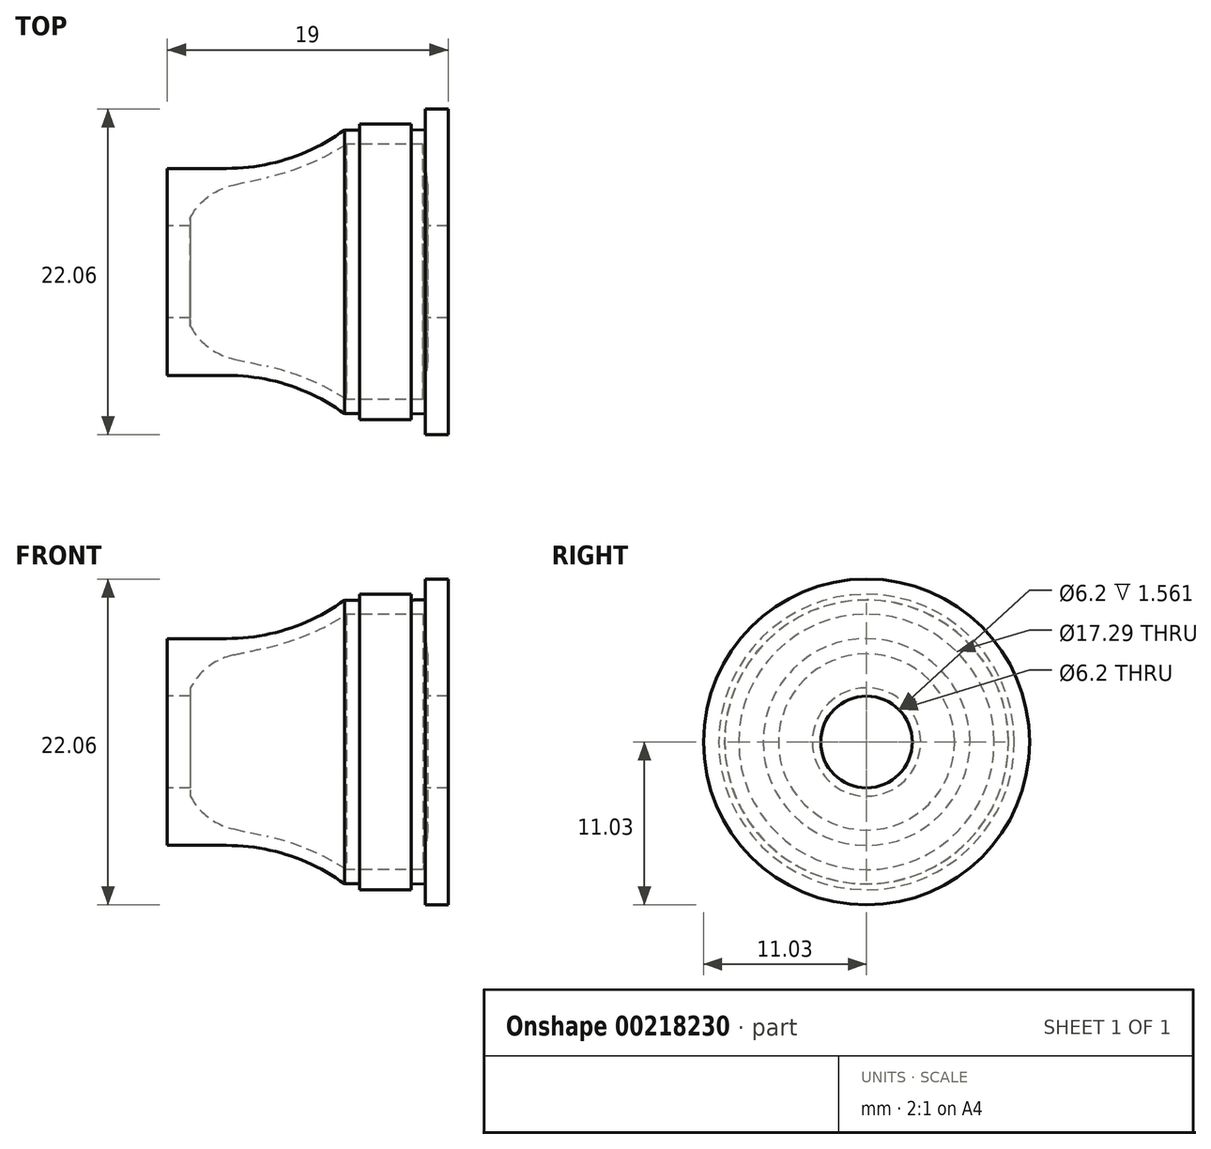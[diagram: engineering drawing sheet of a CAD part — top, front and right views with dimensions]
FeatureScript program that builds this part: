
annotation { "Feature Type Name" : "Feature", "Feature Type Description" : "" }
export const myFeature = defineFeature(function(context is Context, id is Id, definition is map)
    precondition{}
    {
        {
            var Q0;
            Q0=qCreatedBy(makeId("Top.planeOp"),FACE);
            var sketch = newSketch(context, id + "F0", { "sketchPlane" : qUnion([Q0])});
            skLineSegment(sketch, "E0", {"start": v(0, 7) * mm, "end": v(4.01, 7) * mm});
            skLineSegment(sketch, "E1", {"start": v(12, 9.6) * mm, "end": v(13, 9.6) * mm});
            skLineSegment(sketch, "E2", {"start": v(19, 11.03) * mm, "end": v(19, 3.1) * mm});
            skLineSegment(sketch, "E3", {"start": v(19, 3.1) * mm, "end": v(17.44, 3.1) * mm});
            skLineSegment(sketch, "E4", {"start": v(0, 3.1) * mm, "end": v(0, 7) * mm});
            skLineSegment(sketch, "E5", {"start": v(-2.93, 0) * mm, "end": v(20.9, 0) * mm, "construction": true});
            skLineSegment(sketch, "E6", {"start": v(0, 3.1) * mm, "end": v(1.56, 3.1) * mm});
            skLineSegment(sketch, "E7", {"start": v(1.56, 3.1) * mm, "end": v(1.56, 3.67) * mm});
            skLineSegment(sketch, "E8", {"start": v(12.14, 8.64) * mm, "end": v(17.3, 8.64) * mm});
            skLineSegment(sketch, "E9", {"start": v(1.56, 3.1) * mm, "end": v(0, 3.1) * mm});
            skLineSegment(sketch, "E10", {"start": v(16.5, 9.6) * mm, "end": v(16.5, 10) * mm});
            skLineSegment(sketch, "E11", {"start": v(16.5, 10) * mm, "end": v(13, 10) * mm});
            skLineSegment(sketch, "E12", {"start": v(13, 10) * mm, "end": v(13, 9.6) * mm});
            skLineSegment(sketch, "E13", {"start": v(16.5, 9.6) * mm, "end": v(17.5, 9.62) * mm});
            skLineSegment(sketch, "E14", {"start": v(4.5, 5.89) * mm, "end": v(6.76, 6.4) * mm});
            skArc(sketch, "E15", {"start": v(4.5, 5.89) * mm, "mid": v(2.78, 5.1) * mm, "end": v(1.56, 3.67) * mm});
            skLineSegment(sketch, "E16", {"start": v(17.63, 5.96) * mm, "end": v(17.44, 3.1) * mm});
            skArc(sketch, "E17", {"start": v(4.01, 7) * mm, "mid": v(8.21, 7.67) * mm, "end": v(12, 9.6) * mm});
            skArc(sketch, "E18", {"start": v(6.76, 6.4) * mm, "mid": v(9.55, 7.28) * mm, "end": v(12.14, 8.64) * mm});
            skLineSegment(sketch, "E19", {"start": v(17.3, 8.64) * mm, "end": v(17.63, 5.96) * mm});
            skLineSegment(sketch, "E20", {"start": v(17.5, 9.62) * mm, "end": v(17.47, 11.03) * mm});
            skLineSegment(sketch, "E21", {"start": v(17.47, 11.03) * mm, "end": v(19, 11.03) * mm});
            skSolve(sketch);
        }
        {
            var Q0;
            Q0=makeQuery(id+"F0.imprint","IMPRINT",FACE,{"disambiguationData":[TD([[makeQuery(id+"F0.imprint","IMPRINT",EDGE,{"derivedFrom":sQuery(id+"F0.wireOp",EDGE,"E0")}),-1.0]])]});
            var Q1;
            Q1=sQuery(id+"F0.wireOp",EDGE,"E5");
            revolve(context, id + "F1", {"entities" : qUnion([Q0]), "axis" : qUnion([Q1]), "revolveType" : RevolveType.FULL});
        }
    });
